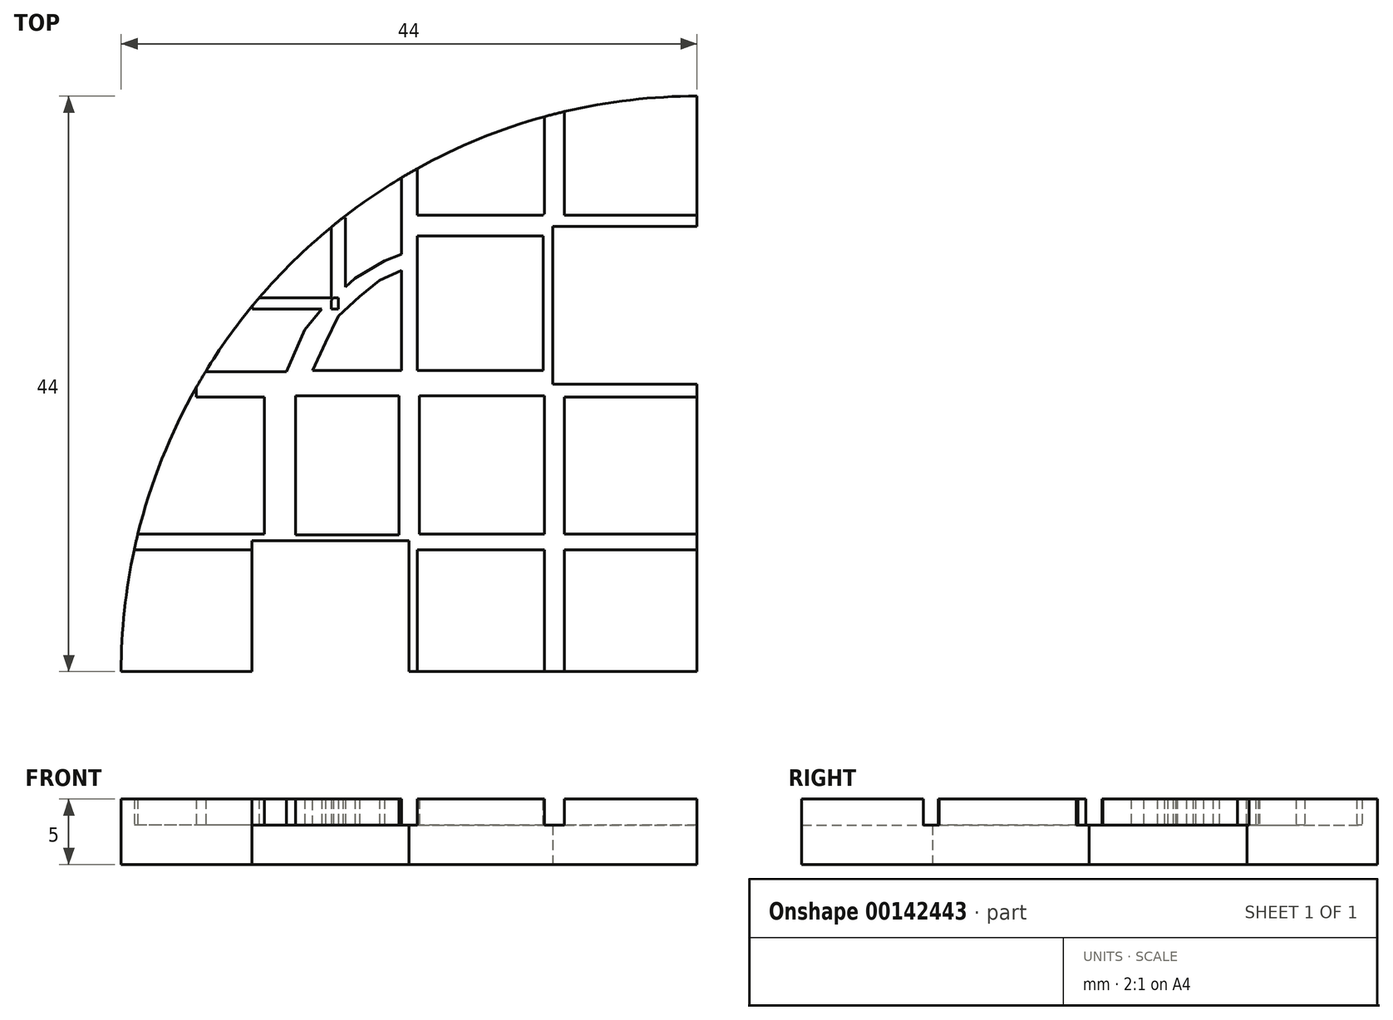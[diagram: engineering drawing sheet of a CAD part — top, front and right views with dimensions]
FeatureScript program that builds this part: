
annotation { "Feature Type Name" : "Feature", "Feature Type Description" : "" }
export const myFeature = defineFeature(function(context is Context, id is Id, definition is map)
    precondition{}
    {
        {
            var Q0;
            Q0=qCreatedBy(makeId("Top.planeOp"),FACE);
            cPlane(context, id + "F0", {"entities" : qUnion([Q0]), "cplaneType" : CPlaneType.OFFSET, "offset" : 3 * mm, "width" : 150 * mm, "height" : 150 * mm});
        }
        {
            var Q0;
            Q0=qCreatedBy(makeId("Top.planeOp"),FACE);
            var sketch = newSketch(context, id + "F1", { "sketchPlane" : qUnion([Q0])});
            skLineSegment(sketch, "E0", {"start": v(0, 0) * mm, "end": v(-22, 0) * mm});
            skLineSegment(sketch, "E1", {"start": v(0, 0) * mm, "end": v(0, 44) * mm});
            skLineSegment(sketch, "E2.bottom", {"start": v(0, 0) * mm, "end": v(-10, 0) * mm});
            skLineSegment(sketch, "E2.top", {"start": v(0, 10) * mm, "end": v(-10, 10) * mm});
            skLineSegment(sketch, "E2.left", {"start": v(0, 0) * mm, "end": v(0, 10) * mm});
            skLineSegment(sketch, "E2.right", {"start": v(-10, 0) * mm, "end": v(-10, 10) * mm});
            skLineSegment(sketch, "E3.bottom", {"start": v(-10, 10) * mm, "end": v(0, 10) * mm});
            skLineSegment(sketch, "E3.top", {"start": v(-10, 22) * mm, "end": v(0, 22) * mm});
            skLineSegment(sketch, "E3.left", {"start": v(-10, 10) * mm, "end": v(-10, 22) * mm});
            skLineSegment(sketch, "E3.right", {"start": v(0, 10) * mm, "end": v(0, 22) * mm});
            skLineSegment(sketch, "E4.top", {"start": v(-10, 32.98) * mm, "end": v(0, 32.98) * mm});
            skLineSegment(sketch, "E4.left", {"start": v(-10, 22) * mm, "end": v(-10, 32.98) * mm});
            skLineSegment(sketch, "E4.right", {"start": v(0, 22) * mm, "end": v(0, 32.98) * mm});
            skLineSegment(sketch, "E5.right", {"start": v(0, 44) * mm, "end": v(0, 44) * mm});
            skLineSegment(sketch, "E6.bottom", {"start": v(-10, 10) * mm, "end": v(-22, 10) * mm});
            skLineSegment(sketch, "E6.top", {"start": v(-10, 0) * mm, "end": v(-22, 0) * mm});
            skLineSegment(sketch, "E6.left", {"start": v(-10, 10) * mm, "end": v(-10, 0) * mm});
            skLineSegment(sketch, "E6.right", {"start": v(-22, 10) * mm, "end": v(-22, 0) * mm});
            skLineSegment(sketch, "E7.bottom", {"start": v(-22, 10) * mm, "end": v(-34, 10) * mm});
            skLineSegment(sketch, "E7.right", {"start": v(-34, 10) * mm, "end": v(-34, 0) * mm});
            skLineSegment(sketch, "E8.bottom", {"start": v(-34, 10) * mm, "end": v(-42, 10) * mm});
            skLineSegment(sketch, "E8.top", {"start": v(-34, 0) * mm, "end": v(-44, 0) * mm});
            skLineSegment(sketch, "E9.bottom", {"start": v(-22, 10) * mm, "end": v(-10, 10) * mm});
            skLineSegment(sketch, "E9.top", {"start": v(-22, 22) * mm, "end": v(-10, 22) * mm});
            skLineSegment(sketch, "E9.left", {"start": v(-22, 10) * mm, "end": v(-22, 22) * mm});
            skLineSegment(sketch, "E10.bottom", {"start": v(-34, 10) * mm, "end": v(-22, 10) * mm});
            skLineSegment(sketch, "E10.top", {"start": v(-34, 22) * mm, "end": v(-22, 22) * mm});
            skLineSegment(sketch, "E10.left", {"start": v(-34, 10) * mm, "end": v(-34, 22) * mm});
            skLineSegment(sketch, "E11.top", {"start": v(-22, 32.98) * mm, "end": v(-10, 32.98) * mm});
            skLineSegment(sketch, "E11.left", {"start": v(-22, 22) * mm, "end": v(-22, 32.98) * mm});
            skLineSegment(sketch, "E12.bottom", {"start": v(-42, 10) * mm, "end": v(-34, 10) * mm});
            skLineSegment(sketch, "E12.top", {"start": v(-38.1, 22) * mm, "end": v(-34, 22) * mm});
            skLineSegment(sketch, "E13.bottom", {"start": v(-38.1, 22) * mm, "end": v(-30.34, 22) * mm});
            skPoint(sketch, "E14.startSnap0", {"position": v(-35.2, 22) * mm});
            skLineSegment(sketch, "E15", {"start": v(-42, 10) * mm, "end": v(-42.84, 10.04) * mm});
            skLineSegment(sketch, "E16.bottom", {"start": v(0, 22) * mm, "end": v(10, 22) * mm});
            skLineSegment(sketch, "E16.top", {"start": v(0, 32.98) * mm, "end": v(10, 32.98) * mm});
            skLineSegment(sketch, "E16.right", {"start": v(10, 22) * mm, "end": v(10, 32.98) * mm});
            skArc(sketch, "E17", {"start": v(0, 44) * mm, "mid": v(-31.11, 31.11) * mm, "end": v(-44, 0) * mm});
            skPoint(sketch, "E18.orphan", {"position": v(-36.4, 22) * mm});
            skPoint(sketch, "E14.start.orphan", {"position": v(-35.2, 26.29) * mm});
            skLineSegment(sketch, "E19", {"start": v(-10, 32.98) * mm, "end": v(-10, 42.85) * mm});
            skLineSegment(sketch, "E20", {"start": v(0, 32.98) * mm, "end": v(0, 44) * mm});
            skLineSegment(sketch, "E21", {"start": v(-22, 32.98) * mm, "end": v(-22, 38.1) * mm});
            skFitSpline(sketch, "E22", {"points": [v(-30.34, 22) * mm, v(-27.44, 28.13) * mm, v(-22, 31.6) * mm], "startDerivative": vector(4.38, 13.4) * mm, "endDerivative": vector(12.33, 5.75) * mm});
            skLineSegment(sketch, "E23", {"start": v(-27.44, 28.13) * mm, "end": v(-33.83, 28.13) * mm});
            skLineSegment(sketch, "E24", {"start": v(-27.44, 28.13) * mm, "end": v(-27.44, 34.4) * mm});
            skSolve(sketch);
        }
        {
            var Q0;
            Q0=qSketchRegion(id+"F1",true);
            var Q1;
            {var subQ0=sQuery(id+"F1.wireOp",EDGE,"E10.top");Q1=makeQuery(id+"F1.imprint","IMPRINT",FACE,{"disambiguationData":[TD([[makeQuery(id+"F1.imprint","IMPRINT",EDGE,{"derivedFrom":subQ0}),1.0]])]});}
            var Q2;
            Q2=makeQuery(id+"F1.imprint","IMPRINT",FACE,{"disambiguationData":[TD([[makeQuery(id+"F1.imprint","IMPRINT",EDGE,{"derivedFrom":sQuery(id+"F1.wireOp",EDGE,"E9.top")}),1.0]])]});
            var Q3;
            Q3=makeQuery(id+"F1.imprint","IMPRINT",FACE,{"disambiguationData":[TD([[makeQuery(id+"F1.imprint","IMPRINT",EDGE,{"derivedFrom":sQuery(id+"F1.wireOp",EDGE,"E9.bottom")}),1.0]])]});
            var Q4;
            Q4=makeQuery(id+"F1.imprint","IMPRINT",FACE,{"disambiguationData":[TD([[makeQuery(id+"F1.imprint","IMPRINT",EDGE,{"derivedFrom":sQuery(id+"F1.wireOp",EDGE,"E10.bottom")}),1.0]])]});
            extrude(context, id + "F2", {"entities" : qUnion([Q0, Q1, Q2, Q3, Q4]), "depth" : 5 * mm});
        }
        {
            var Q0;
            Q0=qCreatedBy(id+"F0.planeOp",FACE);
            var sketch = newSketch(context, id + "F3", { "sketchPlane" : qUnion([Q0])});
            skLineSegment(sketch, "E25", {"start": v(-33.07, 0) * mm, "end": v(-33.07, 22.94) * mm});
            skLineSegment(sketch, "E26", {"start": v(-33.07, 22.94) * mm, "end": v(-30.69, 22.94) * mm});
            skLineSegment(sketch, "E27", {"start": v(-30.69, 22.94) * mm, "end": v(-30.69, 0) * mm});
            skLineSegment(sketch, "E28", {"start": v(-30.69, 0) * mm, "end": v(-33.07, 0) * mm});
            skLineSegment(sketch, "E29.bottom", {"start": v(-22.58, 0) * mm, "end": v(-21.39, 0) * mm});
            skLineSegment(sketch, "E29.top", {"start": v(-22.58, 38.74) * mm, "end": v(-21.39, 38.74) * mm});
            skLineSegment(sketch, "E29.left", {"start": v(-22.58, 0) * mm, "end": v(-22.58, 38.74) * mm});
            skLineSegment(sketch, "E29.right", {"start": v(-21.39, 0) * mm, "end": v(-21.39, 38.74) * mm});
            skLineSegment(sketch, "E30.bottom", {"start": v(-11.65, 0) * mm, "end": v(-10.13, 0) * mm});
            skLineSegment(sketch, "E30.top", {"start": v(-11.65, 43.5) * mm, "end": v(-10.13, 43.5) * mm});
            skLineSegment(sketch, "E30.left", {"start": v(-11.65, 0) * mm, "end": v(-11.65, 43.5) * mm});
            skLineSegment(sketch, "E30.right", {"start": v(-10.13, 0) * mm, "end": v(-10.13, 43.5) * mm});
            skLineSegment(sketch, "E31.bottom", {"start": v(0, 9.3) * mm, "end": v(-43.24, 9.3) * mm});
            skLineSegment(sketch, "E31.top", {"start": v(0, 10.5) * mm, "end": v(-43.24, 10.5) * mm});
            skLineSegment(sketch, "E31.left", {"start": v(0, 9.3) * mm, "end": v(0, 10.5) * mm});
            skLineSegment(sketch, "E31.right", {"start": v(-43.24, 9.3) * mm, "end": v(-43.24, 10.5) * mm});
            skPoint(sketch, "E32.oppositeSnap0", {"position": v(-31.88, 22.94) * mm});
            skLineSegment(sketch, "E32.bottom", {"start": v(0, 21) * mm, "end": v(-38.26, 21) * mm});
            skLineSegment(sketch, "E32.top", {"start": v(0, 22.94) * mm, "end": v(-38.26, 22.94) * mm});
            skLineSegment(sketch, "E32.left", {"start": v(0, 21) * mm, "end": v(0, 22.94) * mm});
            skLineSegment(sketch, "E32.right", {"start": v(-38.26, 21) * mm, "end": v(-38.26, 22.94) * mm});
            skLineSegment(sketch, "E33.bottom", {"start": v(-1.04, 22.94) * mm, "end": v(1.01, 22.94) * mm});
            skLineSegment(sketch, "E33.top", {"start": v(-1.04, 34.2) * mm, "end": v(1.01, 34.2) * mm});
            skLineSegment(sketch, "E33.left", {"start": v(-1.04, 22.94) * mm, "end": v(-1.04, 34.2) * mm});
            skLineSegment(sketch, "E33.right", {"start": v(1.01, 22.94) * mm, "end": v(1.01, 34.2) * mm});
            skLineSegment(sketch, "E34.bottom", {"start": v(1.01, 22.94) * mm, "end": v(-1.04, 22.94) * mm});
            skLineSegment(sketch, "E34.top", {"start": v(1.01, 21) * mm, "end": v(-1.04, 21) * mm});
            skLineSegment(sketch, "E34.left", {"start": v(1.01, 22.94) * mm, "end": v(1.01, 21) * mm});
            skLineSegment(sketch, "E34.right", {"start": v(-1.04, 22.94) * mm, "end": v(-1.04, 21) * mm});
            skPoint(sketch, "E35.oppositeSnap0", {"position": v(-0.02, 34.2) * mm});
            skLineSegment(sketch, "E35.bottom", {"start": v(-22.58, 34.9) * mm, "end": v(-0.02, 34.9) * mm});
            skLineSegment(sketch, "E35.top", {"start": v(-22.58, 33.3) * mm, "end": v(-0.02, 33.3) * mm});
            skLineSegment(sketch, "E35.left", {"start": v(-22.58, 34.9) * mm, "end": v(-22.58, 33.3) * mm});
            skLineSegment(sketch, "E35.right", {"start": v(-0.02, 34.9) * mm, "end": v(-0.02, 33.3) * mm});
            skLineSegment(sketch, "E36.bottom", {"start": v(-27.41, 27.71) * mm, "end": v(-33.97, 27.71) * mm});
            skLineSegment(sketch, "E36.top", {"start": v(-27.41, 28.56) * mm, "end": v(-33.97, 28.56) * mm});
            skLineSegment(sketch, "E36.left", {"start": v(-27.41, 27.71) * mm, "end": v(-27.41, 28.56) * mm});
            skLineSegment(sketch, "E36.right", {"start": v(-33.97, 27.71) * mm, "end": v(-33.97, 28.56) * mm});
            skLineSegment(sketch, "E37.bottom", {"start": v(-26.87, 27.71) * mm, "end": v(-27.96, 27.71) * mm});
            skLineSegment(sketch, "E37.top", {"start": v(-26.87, 34.7) * mm, "end": v(-27.96, 34.7) * mm});
            skLineSegment(sketch, "E37.left", {"start": v(-26.87, 27.71) * mm, "end": v(-26.87, 34.7) * mm});
            skLineSegment(sketch, "E37.right", {"start": v(-27.96, 27.71) * mm, "end": v(-27.96, 34.7) * mm});
            skLineSegment(sketch, "E38", {"start": v(-31.36, 22.94) * mm, "end": v(-29.96, 26.13) * mm});
            skLineSegment(sketch, "E39", {"start": v(-29.96, 26.13) * mm, "end": v(-28.69, 27.71) * mm});
            skLineSegment(sketch, "E40", {"start": v(-28.69, 27.71) * mm, "end": v(-26.14, 30.08) * mm});
            skLineSegment(sketch, "E41", {"start": v(-26.14, 30.08) * mm, "end": v(-23.9, 31.42) * mm});
            skLineSegment(sketch, "E42", {"start": v(-23.9, 31.42) * mm, "end": v(-22.58, 31.9) * mm});
            skLineSegment(sketch, "E43", {"start": v(-22.58, 31.9) * mm, "end": v(-22.58, 30.69) * mm});
            skLineSegment(sketch, "E44", {"start": v(-22.58, 30.69) * mm, "end": v(-24.26, 29.9) * mm});
            skLineSegment(sketch, "E45", {"start": v(-24.26, 29.9) * mm, "end": v(-25.77, 28.68) * mm});
            skLineSegment(sketch, "E46", {"start": v(-25.77, 28.68) * mm, "end": v(-27.41, 27.16) * mm});
            skLineSegment(sketch, "E47", {"start": v(-27.41, 27.16) * mm, "end": v(-28.39, 25.16) * mm});
            skLineSegment(sketch, "E48", {"start": v(-28.39, 25.16) * mm, "end": v(-29.42, 22.94) * mm});
            skPoint(sketch, "E49.firstSnap0", {"position": v(-31.88, 0) * mm});
            skLineSegment(sketch, "E49.bottom", {"start": v(-31.88, -0.88) * mm, "end": v(-21.39, -0.88) * mm});
            skLineSegment(sketch, "E49.top", {"start": v(-31.88, 0.8) * mm, "end": v(-21.39, 0.8) * mm});
            skLineSegment(sketch, "E49.left", {"start": v(-31.88, -0.88) * mm, "end": v(-31.88, 0.8) * mm});
            skLineSegment(sketch, "E49.right", {"start": v(-21.39, -0.88) * mm, "end": v(-21.39, 0.8) * mm});
            skSolve(sketch);
        }
        {
            var Q0;
            Q0=qSketchRegion(id+"F3",true);
            extrude(context, id + "F4", {"entities" : qUnion([Q0]), "operationType" : NewBodyOperationType.REMOVE, "depth" : 25 * mm});
        }
        {
            var Q0;
            Q0=qCreatedBy(id+"F0.planeOp",FACE);
            var sketch = newSketch(context, id + "F5", { "sketchPlane" : qUnion([Q0])});
            skLineSegment(sketch, "E50.bottom", {"start": v(-30.86, 23.03) * mm, "end": v(-10.21, 23.03) * mm});
            skLineSegment(sketch, "E50.top", {"start": v(-30.86, 21.1) * mm, "end": v(-10.21, 21.1) * mm});
            skLineSegment(sketch, "E50.left", {"start": v(-30.86, 23.03) * mm, "end": v(-30.86, 21.1) * mm});
            skLineSegment(sketch, "E50.right", {"start": v(-10.21, 23.03) * mm, "end": v(-10.21, 21.1) * mm});
            skLineSegment(sketch, "E51.bottom", {"start": v(-22.76, 9.39) * mm, "end": v(-21.21, 9.39) * mm});
            skLineSegment(sketch, "E51.top", {"start": v(-22.76, 23.03) * mm, "end": v(-21.21, 23.03) * mm});
            skLineSegment(sketch, "E51.left", {"start": v(-22.76, 9.39) * mm, "end": v(-22.76, 23.03) * mm});
            skLineSegment(sketch, "E51.right", {"start": v(-21.21, 9.39) * mm, "end": v(-21.21, 23.03) * mm});
            skLineSegment(sketch, "E52.bottom", {"start": v(-11.75, 23.03) * mm, "end": v(-10.21, 23.03) * mm});
            skLineSegment(sketch, "E52.top", {"start": v(-11.75, 35) * mm, "end": v(-10.21, 35) * mm});
            skLineSegment(sketch, "E52.left", {"start": v(-11.75, 23.03) * mm, "end": v(-11.75, 35) * mm});
            skLineSegment(sketch, "E52.right", {"start": v(-10.21, 23.03) * mm, "end": v(-10.21, 35) * mm});
            skLineSegment(sketch, "E53.bottom", {"start": v(-22.76, 9.39) * mm, "end": v(-33.06, 9.39) * mm});
            skLineSegment(sketch, "E53.top", {"start": v(-22.76, 10.44) * mm, "end": v(-33.06, 10.44) * mm});
            skLineSegment(sketch, "E53.left", {"start": v(-22.76, 9.39) * mm, "end": v(-22.76, 10.44) * mm});
            skLineSegment(sketch, "E53.right", {"start": v(-33.06, 9.39) * mm, "end": v(-33.06, 10.44) * mm});
            skSolve(sketch);
        }
        {
            var Q0;
            Q0=qSketchRegion(id+"F5",true);
            extrude(context, id + "F6", {"entities" : qUnion([Q0]), "operationType" : NewBodyOperationType.REMOVE, "depth" : 25 * mm});
        }
        {
            var Q0;
            Q0=qCreatedBy(makeId("Top.planeOp"),FACE);
            var sketch = newSketch(context, id + "F7", { "sketchPlane" : qUnion([Q0])});
            skLineSegment(sketch, "E54.bottom", {"start": v(-32, -10) * mm, "end": v(-22, -10) * mm});
            skLineSegment(sketch, "E54.top", {"start": v(-32, 10) * mm, "end": v(-22, 10) * mm});
            skLineSegment(sketch, "E54.left", {"start": v(-32, -10) * mm, "end": v(-32, 10) * mm});
            skLineSegment(sketch, "E54.right", {"start": v(-22, -10) * mm, "end": v(-22, 10) * mm});
            skLineSegment(sketch, "E55.bottom", {"start": v(-11.04, 21.97) * mm, "end": v(10, 21.97) * mm});
            skLineSegment(sketch, "E55.top", {"start": v(-11.04, 34.04) * mm, "end": v(10, 34.04) * mm});
            skLineSegment(sketch, "E55.left", {"start": v(-11.04, 21.97) * mm, "end": v(-11.04, 34.04) * mm});
            skLineSegment(sketch, "E55.right", {"start": v(10, 21.97) * mm, "end": v(10, 34.04) * mm});
            skSolve(sketch);
        }
        {
            var Q0;
            Q0 = qSketchRegion(id + "F7", true);
            extrude(context, id + "F8", {"entities" : qUnion([Q0]), "operationType" : NewBodyOperationType.REMOVE, "depth" : 25 * mm});
        }
    });
